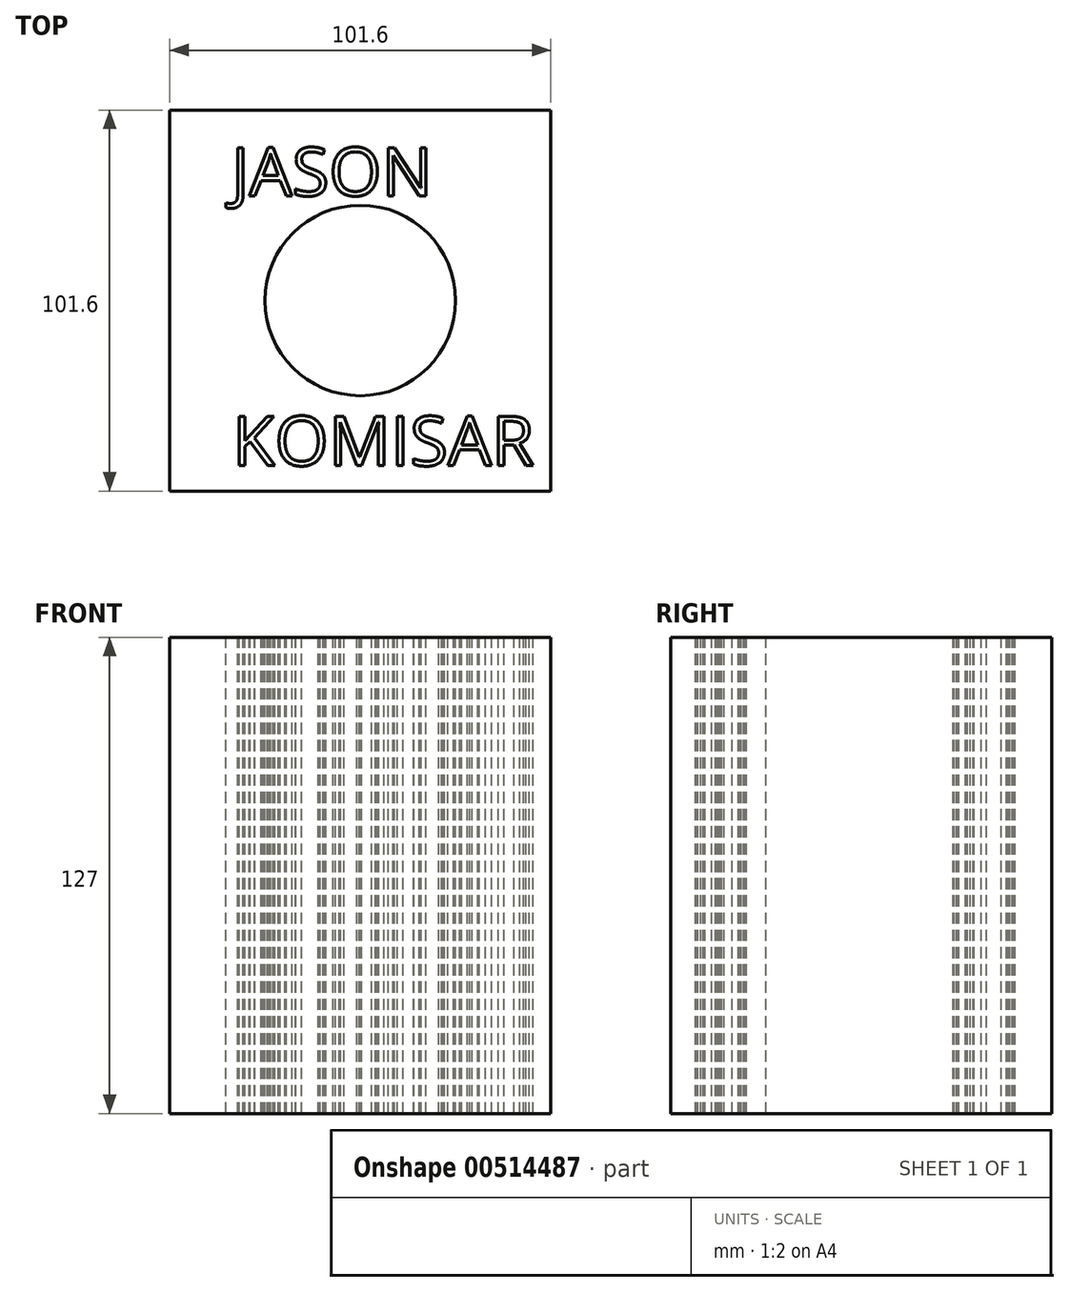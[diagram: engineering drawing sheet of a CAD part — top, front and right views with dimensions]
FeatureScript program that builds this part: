
annotation { "Feature Type Name" : "Feature", "Feature Type Description" : "" }
export const myFeature = defineFeature(function(context is Context, id is Id, definition is map)
    precondition{}
    {
        {
            var Q0;
            Q0=qCreatedBy(makeId("Top.planeOp"),FACE);
            var sketch = newSketch(context, id + "F0", { "sketchPlane" : qUnion([Q0])});
            skLineSegment(sketch, "E0.bottom", {"start": v(50.8, 50.8) * mm, "end": v(-50.8, 50.8) * mm});
            skLineSegment(sketch, "E0.top", {"start": v(50.8, -50.8) * mm, "end": v(-50.8, -50.8) * mm});
            skLineSegment(sketch, "E0.left", {"start": v(50.8, 50.8) * mm, "end": v(50.8, -50.8) * mm});
            skLineSegment(sketch, "E0.right", {"start": v(-50.8, 50.8) * mm, "end": v(-50.8, -50.8) * mm});
            skPoint(sketch, "E0.middle", {"position": v(0, 0) * mm});
            skSolve(sketch);
        }
        {
            var Q0;
            Q0 = qSketchRegion(id + "F0", true);
            extrude(context, id + "F1", {"entities" : qUnion([Q0]), "depth" : 101.6 * mm});
        }
        {
            var Q0;
            Q0=makeQuery(id+"F1.opExtrude","CAP_FACE",FACE,{"disambiguationData":[OSD([sQuery(id+"F0.wireOp",EDGE,"E0.bottom"),sQuery(id+"F0.wireOp",EDGE,"E0.top"),sQuery(id+"F0.wireOp",EDGE,"E0.left"),sQuery(id+"F0.wireOp",EDGE,"E0.right")])],"isStart":false});
            var sketch = newSketch(context, id + "F2", { "sketchPlane" : qUnion([Q0])});
            skCircle(sketch, "E1", {"center": v(0, 0) * mm, "radius": 25.4 * mm});
            skSolve(sketch);
        }
        {
            var Q0;
            Q0=makeQuery(id+"F2.imprint","IMPRINT",FACE,{"disambiguationData":[TD([[makeQuery(id+"F2.imprint","IMPRINT",EDGE,{"derivedFrom":sQuery(id+"F2.wireOp",EDGE,"E1")}),1.0]])]});
            extrude(context, id + "F3", {"entities" : qUnion([Q0]), "operationType" : NewBodyOperationType.REMOVE, "oppositeDirection" : true, "depth" : 101.6 * mm});
        }
        {
            var Q0;
            Q0=makeQuery(id+"F1.opExtrude","CAP_FACE",FACE,{"disambiguationData":[OSD([sQuery(id+"F0.wireOp",EDGE,"E0.bottom"),sQuery(id+"F0.wireOp",EDGE,"E0.top"),sQuery(id+"F0.wireOp",EDGE,"E0.left"),sQuery(id+"F0.wireOp",EDGE,"E0.right")])],"isStart":false});
            extrude(context, id + "F4", {"entities" : qUnion([Q0]), "operationType" : NewBodyOperationType.ADD, "depth" : 25.4 * mm});
        }
        {
            var Q0;
            Q0=makeQuery(id+"F4.opExtrude","CAP_FACE",FACE,{"disambiguationData":[OSD([sQuery(id+"F0.wireOp",EDGE,"E0.bottom"),sQuery(id+"F0.wireOp",EDGE,"E0.top"),sQuery(id+"F0.wireOp",EDGE,"E0.left"),sQuery(id+"F0.wireOp",EDGE,"E0.right")])],"isStart":false});
            var sketch = newSketch(context, id + "F5", { "sketchPlane" : qUnion([Q0])});
            skText(sketch, "E2", { "text": "JASON\n", "fontName": "OpenSans-Regular.ttf"});
            skText(sketch, "E3", { "text": "KOMISAR", "fontName": "OpenSans-Regular.ttf"});
            const initialGuessF5  = {"E2": [-0.0344, 0.02792, 1, 0, 0.01295], "E3": [-0.0341, -0.04403, 1, 0, 0.01324]};
            skSetInitialGuess(sketch, initialGuessF5);
            skSolve(sketch);
        }
        {
            var Q0;
            Q0 = qSketchRegion(id + "F5", true);
            extrude(context, id + "F6", {"entities" : qUnion([Q0]), "operationType" : NewBodyOperationType.REMOVE, "oppositeDirection" : true, "depth" : 152.4 * mm});
        }
    });
